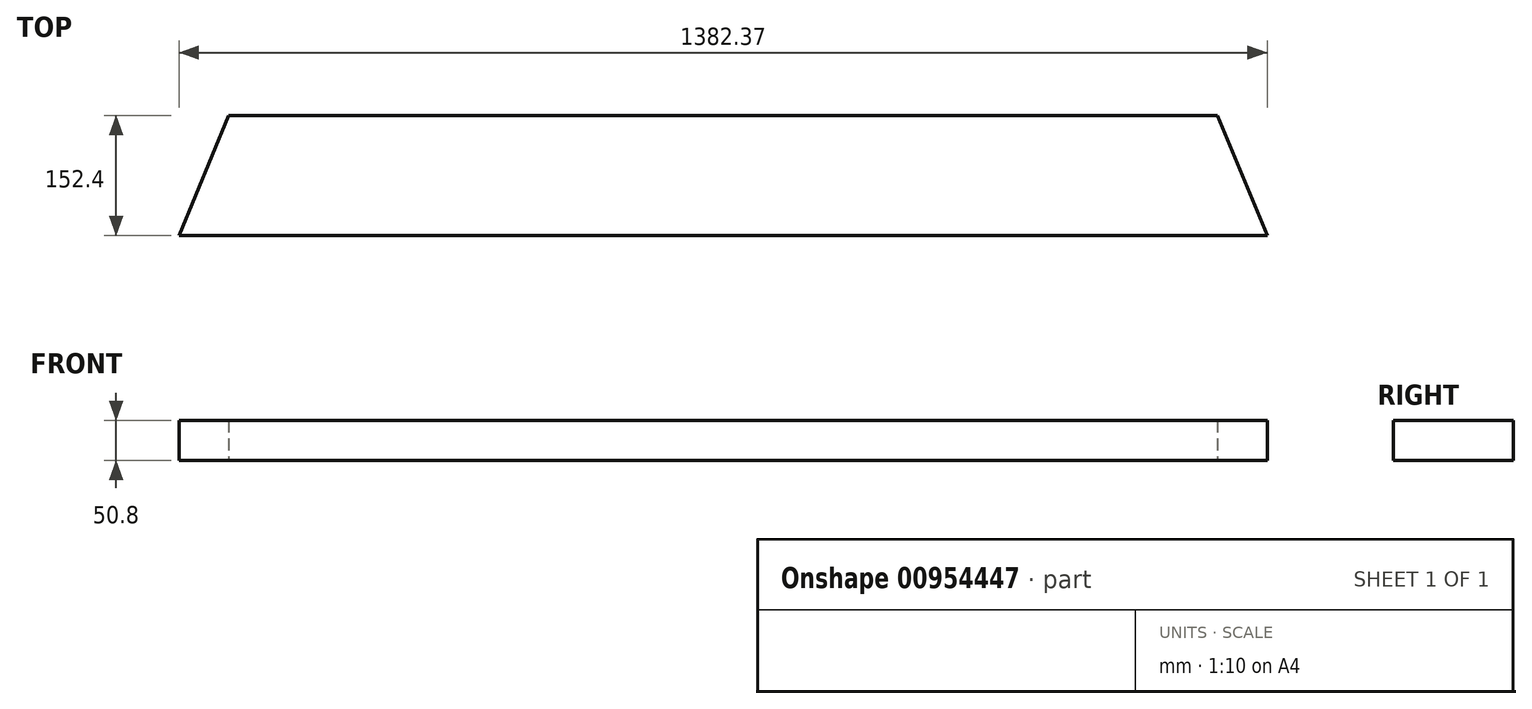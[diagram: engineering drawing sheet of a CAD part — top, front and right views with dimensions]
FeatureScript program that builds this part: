
annotation { "Feature Type Name" : "Feature", "Feature Type Description" : "" }
export const myFeature = defineFeature(function(context is Context, id is Id, definition is map)
    precondition{}
    {
        {
            var Q0;
            Q0=qCreatedBy(makeId("Top.planeOp"),FACE);
            var sketch = newSketch(context, id + "F0", { "sketchPlane" : qUnion([Q0])});
            skLineSegment(sketch, "E0", {"start": v(0, 0) * mm, "end": v(1382.37, 0) * mm});
            skLineSegment(sketch, "E1", {"start": v(1382.37, 0) * mm, "end": v(1319.24, 152.4) * mm});
            skLineSegment(sketch, "E2", {"start": v(1319.24, 152.4) * mm, "end": v(63.13, 152.4) * mm});
            skLineSegment(sketch, "E3", {"start": v(63.13, 152.4) * mm, "end": v(0, 0) * mm});
            skSolve(sketch);
        }
        {
            var Q0;
            Q0 = qSketchRegion(id + "F0", true);
            extrude(context, id + "F1", {"entities" : qUnion([Q0]), "depth" : 50.8 * mm, "offsetDistance" : 25.4 * mm});
        }
    });
